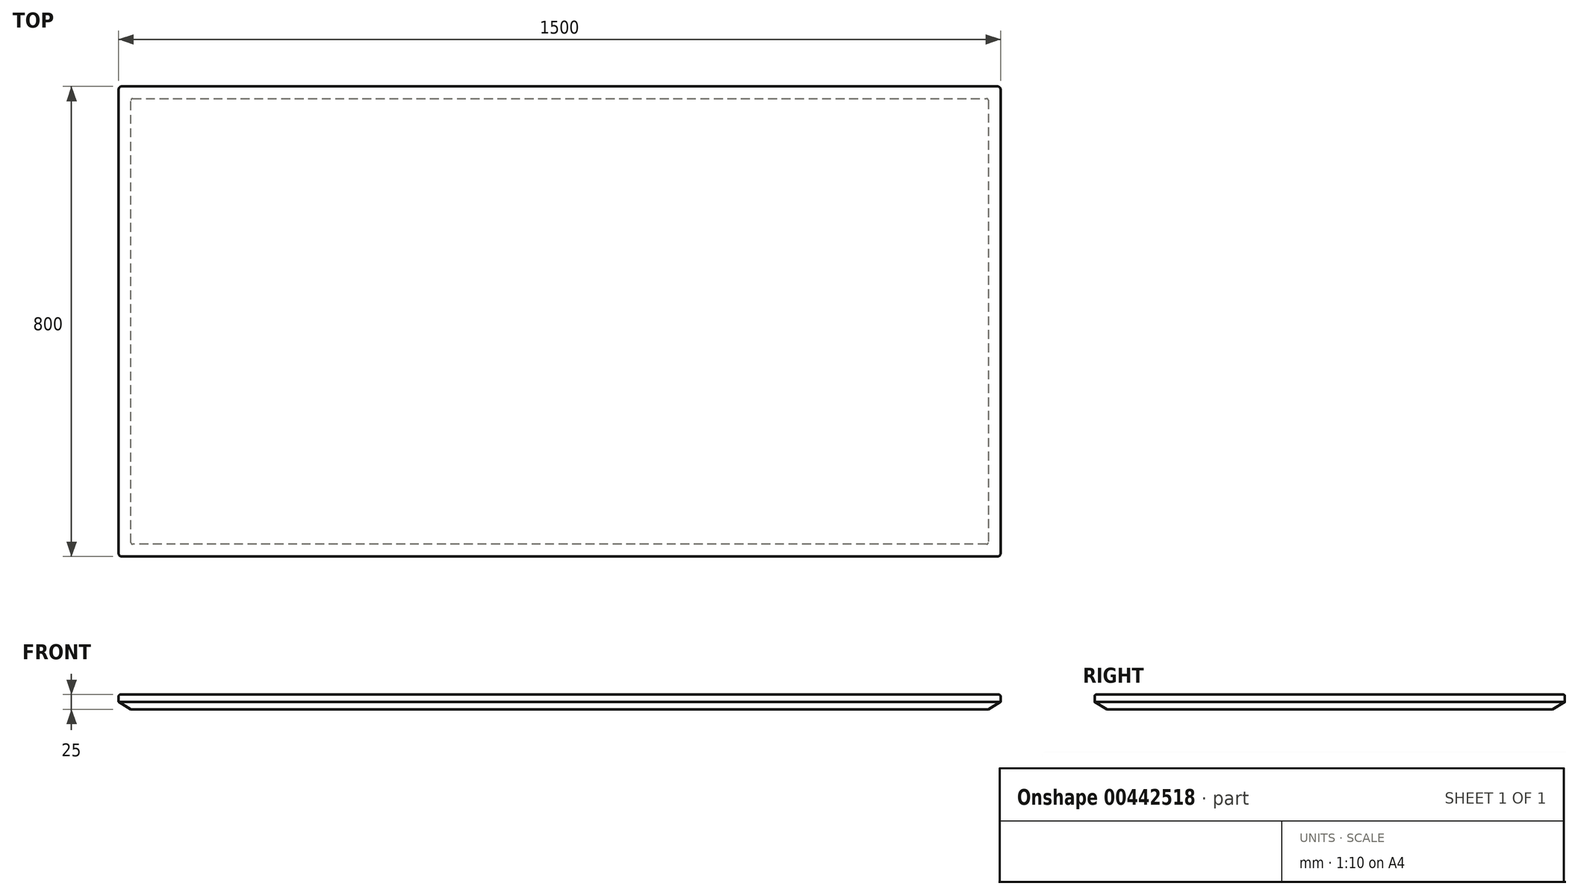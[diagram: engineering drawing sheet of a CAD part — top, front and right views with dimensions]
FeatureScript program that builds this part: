
annotation { "Feature Type Name" : "Feature", "Feature Type Description" : "" }
export const myFeature = defineFeature(function(context is Context, id is Id, definition is map)
    precondition{}
    {
        {
            var Q0;
            Q0=qCreatedBy(makeId("Top.planeOp"),FACE);
            var sketch = newSketch(context, id + "F0", { "sketchPlane" : qUnion([Q0])});
            skLineSegment(sketch, "E0.bottom", {"start": v(0, 0) * mm, "end": v(-1500, 0) * mm});
            skLineSegment(sketch, "E0.top", {"start": v(0, 800) * mm, "end": v(-1500, 800) * mm});
            skLineSegment(sketch, "E0.left", {"start": v(0, 0) * mm, "end": v(0, 800) * mm});
            skLineSegment(sketch, "E0.right", {"start": v(-1500, 0) * mm, "end": v(-1500, 800) * mm});
            skSolve(sketch);
        }
        {
            var Q0;
            Q0 = qSketchRegion(id + "F0", true);
            extrude(context, id + "F1", {"entities" : qUnion([Q0]), "depth" : 25 * mm, "offsetDistance" : 25 * mm});
        }
        {
            var Q0;
            Q0=makeQuery(id+"F1.opExtrude","CAP_FACE",FACE,{"disambiguationData":[OSD([sQuery(id+"F0.wireOp",EDGE,"E0.bottom"),sQuery(id+"F0.wireOp",EDGE,"E0.top"),sQuery(id+"F0.wireOp",EDGE,"E0.left"),sQuery(id+"F0.wireOp",EDGE,"E0.right")])],"isStart":true});
            chamfer(context, id + "F2", {"entities" : qUnion([Q0]), "chamferType" : ChamferType.TWO_OFFSETS, "width1" : 21 * mm, "oppositeDirection" : false, "width2" : 12.5 * mm, "tangentPropagation" : true});
        }
        {
            var Q0;
            Q0=makeQuery(id+"F1.opExtrude","CAP_FACE",FACE,{"disambiguationData":[OSD([sQuery(id+"F0.wireOp",EDGE,"E0.bottom"),sQuery(id+"F0.wireOp",EDGE,"E0.top"),sQuery(id+"F0.wireOp",EDGE,"E0.left"),sQuery(id+"F0.wireOp",EDGE,"E0.right")])],"isStart":false});
            fillet(context, id + "F3", {"entities" : qUnion([Q0]), "radius" : 3 * mm, "tangentPropagation" : true, "allowEdgeOverflow" : false});
        }
        {
            var Q0;
            Q0=makeQuery(id+"F1.opExtrude","SWEPT_EDGE",EDGE,{"disambiguationData":[OSD([sQuery(id+"F0.wireOp",EDGE,"E0.bottom"),sQuery(id+"F0.wireOp",EDGE,"E0.right")])]});
            var Q1;
            Q1=makeQuery(id+"F2.opChamfer","BLEND_EDGE",EDGE,{"blendedFrom":[makeQuery(id+"F1.opExtrude","CAP_EDGE",EDGE,{"disambiguationData":[OSD([sQuery(id+"F0.wireOp",EDGE,"E0.bottom")])],"isStart":true}),makeQuery(id+"F1.opExtrude","CAP_EDGE",EDGE,{"disambiguationData":[OSD([sQuery(id+"F0.wireOp",EDGE,"E0.right")])],"isStart":true})],"blendedInto":[]});
            var Q2;
            Q2=makeQuery(id+"F1.opExtrude","SWEPT_EDGE",EDGE,{"disambiguationData":[OSD([sQuery(id+"F0.wireOp",EDGE,"E0.top"),sQuery(id+"F0.wireOp",EDGE,"E0.right")])]});
            var Q3;
            Q3=makeQuery(id+"F2.opChamfer","BLEND_EDGE",EDGE,{"blendedFrom":[makeQuery(id+"F1.opExtrude","CAP_EDGE",EDGE,{"disambiguationData":[OSD([sQuery(id+"F0.wireOp",EDGE,"E0.top")])],"isStart":true}),makeQuery(id+"F1.opExtrude","CAP_EDGE",EDGE,{"disambiguationData":[OSD([sQuery(id+"F0.wireOp",EDGE,"E0.right")])],"isStart":true})],"blendedInto":[]});
            var Q4;
            Q4=makeQuery(id+"F1.opExtrude","SWEPT_EDGE",EDGE,{"disambiguationData":[OSD([sQuery(id+"F0.wireOp",EDGE,"E0.top"),sQuery(id+"F0.wireOp",EDGE,"E0.left")])]});
            var Q5;
            Q5=makeQuery(id+"F2.opChamfer","BLEND_EDGE",EDGE,{"blendedFrom":[makeQuery(id+"F1.opExtrude","CAP_EDGE",EDGE,{"disambiguationData":[OSD([sQuery(id+"F0.wireOp",EDGE,"E0.top")])],"isStart":true}),makeQuery(id+"F1.opExtrude","CAP_EDGE",EDGE,{"disambiguationData":[OSD([sQuery(id+"F0.wireOp",EDGE,"E0.left")])],"isStart":true})],"blendedInto":[]});
            var Q6;
            Q6=makeQuery(id+"F1.opExtrude","SWEPT_EDGE",EDGE,{"disambiguationData":[OSD([sQuery(id+"F0.wireOp",EDGE,"E0.bottom"),sQuery(id+"F0.wireOp",EDGE,"E0.left")])]});
            var Q7;
            Q7=makeQuery(id+"F2.opChamfer","BLEND_EDGE",EDGE,{"blendedFrom":[makeQuery(id+"F1.opExtrude","CAP_EDGE",EDGE,{"disambiguationData":[OSD([sQuery(id+"F0.wireOp",EDGE,"E0.bottom")])],"isStart":true}),makeQuery(id+"F1.opExtrude","CAP_EDGE",EDGE,{"disambiguationData":[OSD([sQuery(id+"F0.wireOp",EDGE,"E0.left")])],"isStart":true})],"blendedInto":[]});
            fillet(context, id + "F4", {"entities" : qUnion([Q0, Q1, Q2, Q3, Q4, Q5, Q6, Q7]), "radius" : 5 * mm, "tangentPropagation" : true, "allowEdgeOverflow" : false});
        }
    });
